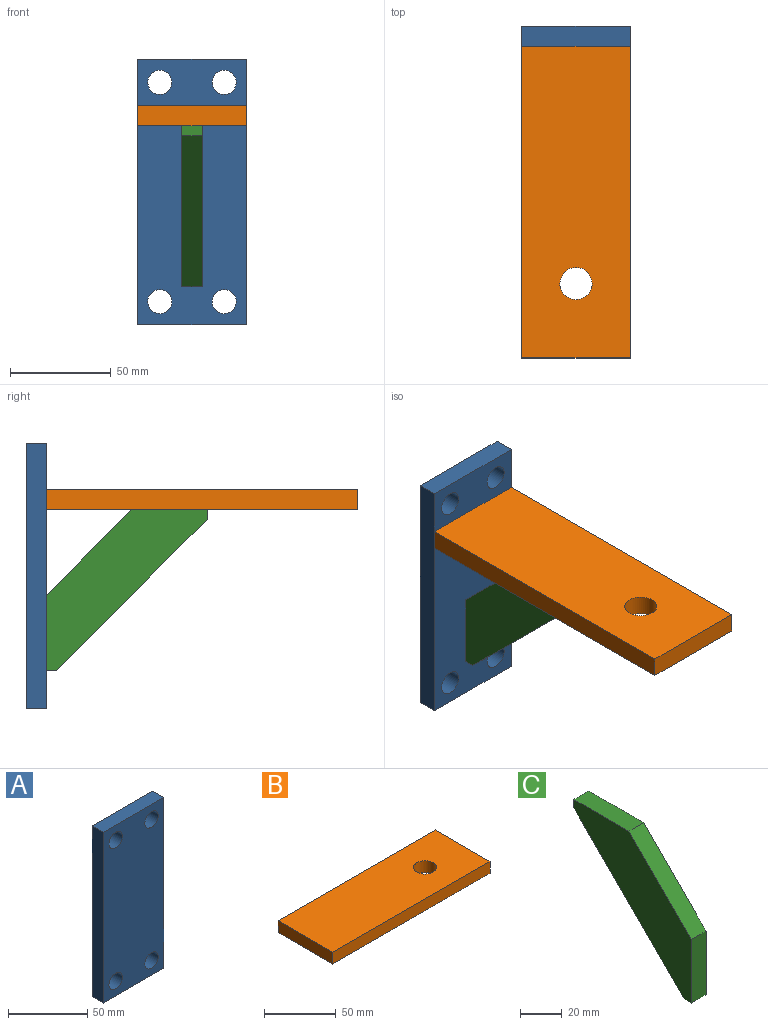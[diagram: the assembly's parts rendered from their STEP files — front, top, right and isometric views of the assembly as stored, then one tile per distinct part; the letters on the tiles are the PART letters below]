
ASSEMBLY  parts=3 mates=2
PART A: 10 faces, bbox 54x10x132 mm
  f0: plane 132x10mm, normal (-1,0,0), area 1320mm2, adj f1,f6,f8,f9
  f1: plane 54x10mm, normal (0,0,-1), area 540mm2, adj f0,f2,f8,f9
  f2: plane 132x10mm, normal (1,0,0), area 1320mm2, adj f1,f6,f8,f9
  f3: cylinder r=6mm len=12mm, axis (0,1,0), area 377mm2, adj f8,f9
  f4: cylinder r=6mm len=12mm, axis (0,1,0), area 377mm2, adj f8,f9
  f5: cylinder r=6mm len=12mm, axis (0,1,0), area 377mm2, adj f8,f9
  f6: plane 54x10mm, normal (0,0,1), area 540mm2, adj f0,f2,f8,f9
  f7: cylinder r=6mm len=12mm, axis (0,1,0), area 377mm2, adj f8,f9
  f8: plane 132x54mm, normal (0,-1,0), area 6675.6mm2, adj f0,f1,f2,f3,f4,f5,f6,f7
  f9: plane 132x54mm, normal (0,1,0), area 6675.6mm2, adj f0,f1,f2,f3,f4,f5,f6,f7
PART B: 7 faces, bbox 155x54x10 mm
  f0: plane 54x10mm, normal (-1,0,0), area 540mm2, adj f1,f3,f5,f6
  f1: plane 155x10mm, normal (0,-1,0), area 1550mm2, adj f0,f2,f5,f6
  f2: plane 54x10mm, normal (1,0,0), area 540mm2, adj f1,f3,f5,f6
  f3: plane 155x10mm, normal (0,1,0), area 1550mm2, adj f0,f2,f5,f6
  f4: cylinder r=8mm len=16mm, axis (0,0,-1), area 502.7mm2, adj f5,f6
  f5: plane 155x54mm, normal (0,0,1), area 8168.9mm2, adj f0,f1,f2,f3,f4
  f6: plane 155x54mm, normal (0,0,-1), area 8168.9mm2, adj f0,f1,f2,f3,f4
PART C: 8 faces, bbox 10x80x80 mm
  f0: plane 37.43x10mm, normal (0,-1,0), area 374.3mm2, adj f1,f5,f6,f7
  f1: plane 10x5mm, normal (0,0,-1), area 50mm2, adj f0,f2,f6,f7
  f2: plane 75x75mm, normal (0,0.71,-0.71), area 1060.7mm2, adj f1,f3,f6,f7
  f3: plane 10x5mm, normal (0,1,0), area 50mm2, adj f2,f4,f6,f7
  f4: plane 37.43x10mm, normal (0,0,1), area 374.3mm2, adj f3,f5,f6,f7
  f5: plane 42.57x42.57mm, normal (0,-0.71,0.71), area 602.1mm2, adj f0,f4,f6,f7
  f6: plane 80x80mm, normal (1,0,0), area 2681.2mm2, adj f0,f1,f2,f3,f4,f5
  f7: plane 80x80mm, normal (-1,0,0), area 2681.2mm2, adj f0,f1,f2,f3,f4,f5
PLACE A t=(6.57,-7.7,8.67)mm
PLACE B rot(axis=(0,0,-1),90deg) t=(6.57,-17.7,107.67)mm
PLACE C rot(axis=(0,0,1),180deg) t=(38.57,-17.7,22.67)mm
MATE fastened C.f4 <-> B.f6  axis (0,0,1) through (33.57,-97.7,107.67)mm
MATE fastened B.f0 <-> A.f8  axis (0,1,0) through (33.57,-17.7,117.67)mm
